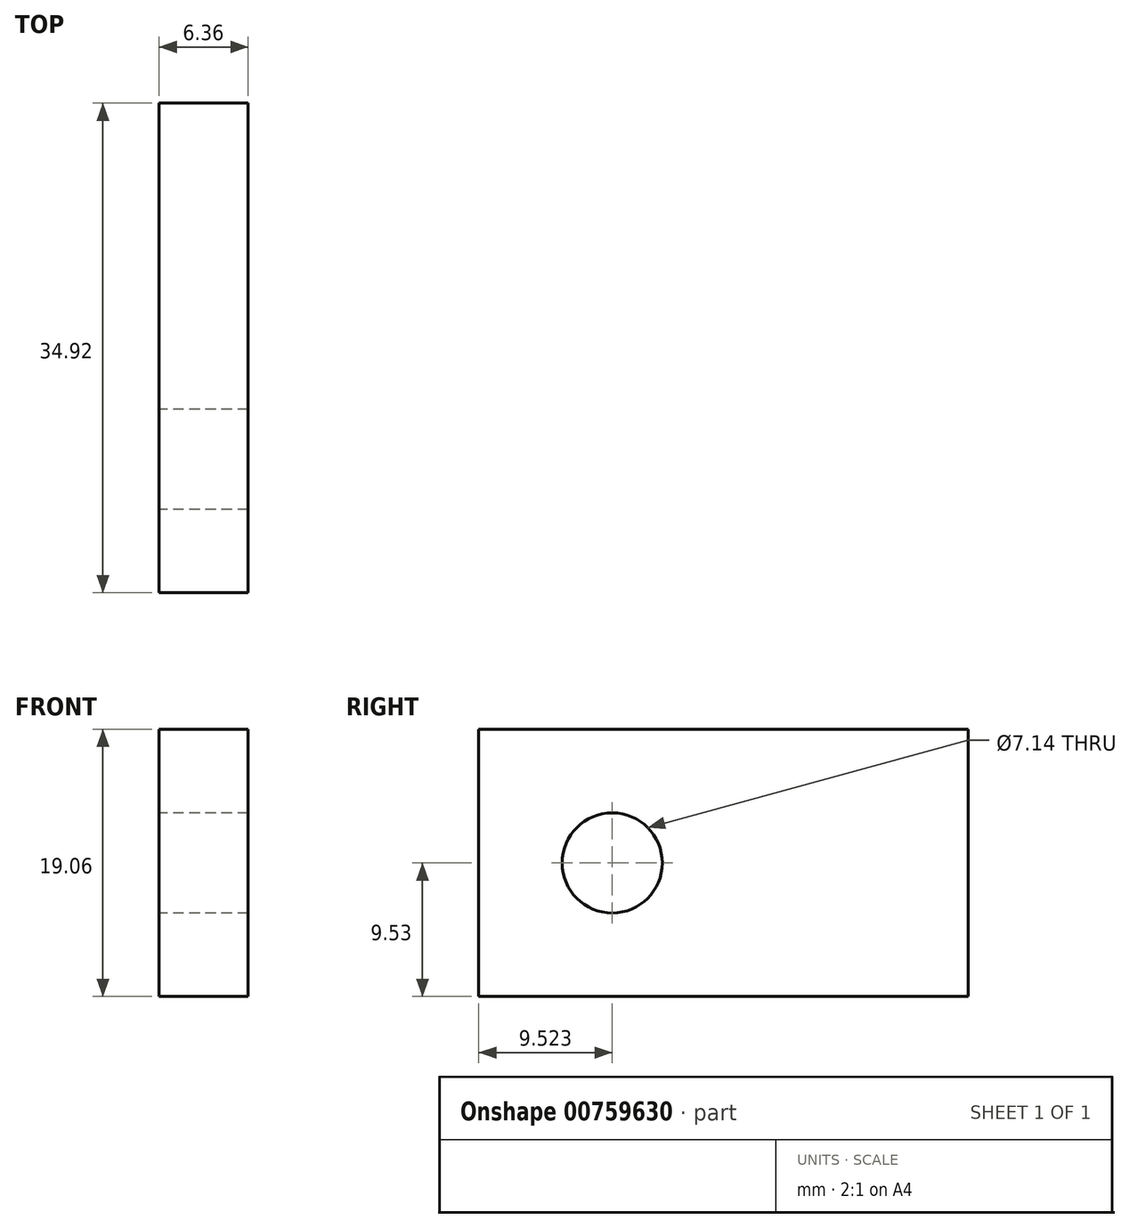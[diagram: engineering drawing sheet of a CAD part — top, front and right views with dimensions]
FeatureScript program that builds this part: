
annotation { "Feature Type Name" : "Feature", "Feature Type Description" : "" }
export const myFeature = defineFeature(function(context is Context, id is Id, definition is map)
    precondition{}
    {
        {
            var Q0;
            Q0=qCreatedBy(makeId("Right.planeOp"),FACE);
            var sketch = newSketch(context, id + "F0", { "sketchPlane" : qUnion([Q0])});
            skLineSegment(sketch, "E0.bottom", {"start": v(17.46, 9.53) * mm, "end": v(-17.46, 9.53) * mm});
            skLineSegment(sketch, "E0.top", {"start": v(17.46, -9.53) * mm, "end": v(-17.46, -9.53) * mm});
            skLineSegment(sketch, "E0.left", {"start": v(17.46, 9.53) * mm, "end": v(17.46, -9.53) * mm});
            skLineSegment(sketch, "E0.right", {"start": v(-17.46, 9.53) * mm, "end": v(-17.46, -9.53) * mm});
            skPoint(sketch, "E0.middle", {"position": v(0, 0) * mm});
            skCircle(sketch, "E1", {"center": v(-7.94, 0) * mm, "radius": 3.57 * mm});
            skSolve(sketch);
        }
        {
            var Q0;
            Q0=makeQuery(id+"F0.imprint","IMPRINT",FACE,{"disambiguationData":[TD([[makeQuery(id+"F0.imprint","IMPRINT",EDGE,{"derivedFrom":sQuery(id+"F0.wireOp",EDGE,"E0.bottom")}),1.0]])]});
            extrude(context, id + "F1", {"entities" : qUnion([Q0]), "endBound" : BoundingType.SYMMETRIC, "depth" : 6.35 * mm, "offsetDistance" : 25.4 * mm});
        }
    });
